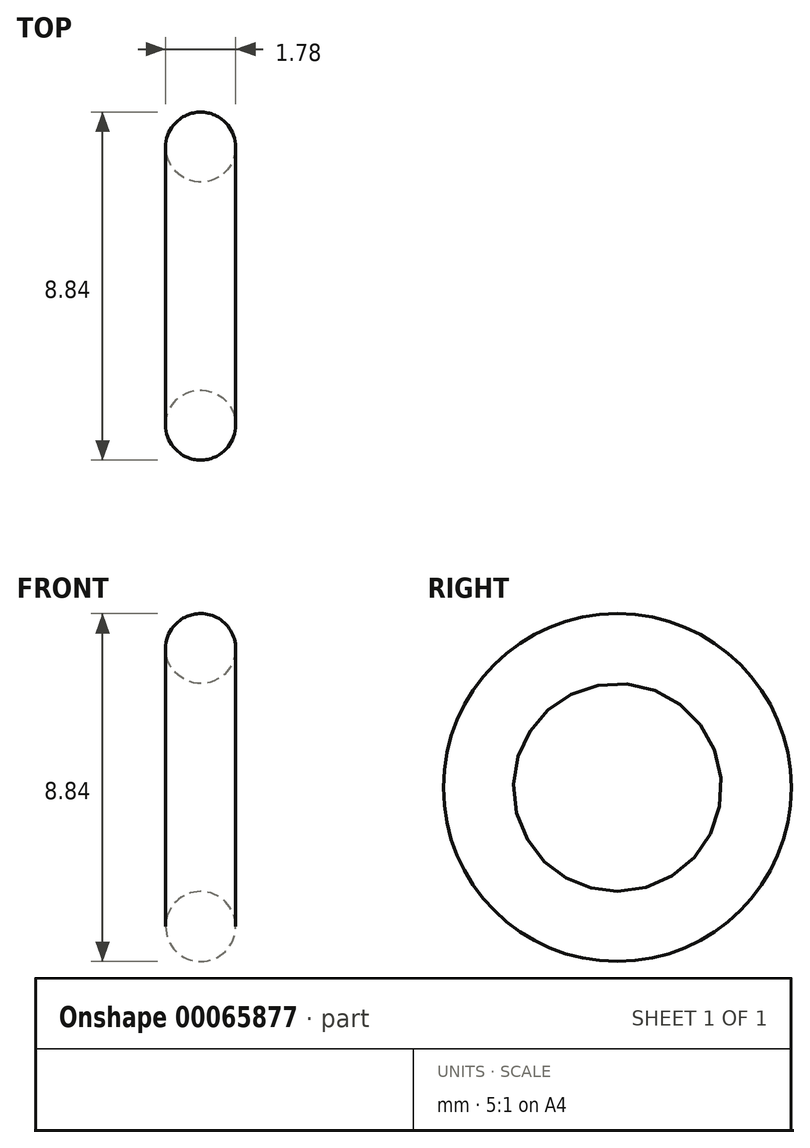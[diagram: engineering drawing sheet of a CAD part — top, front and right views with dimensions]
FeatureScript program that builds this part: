
annotation { "Feature Type Name" : "Feature", "Feature Type Description" : "" }
export const myFeature = defineFeature(function(context is Context, id is Id, definition is map)
    precondition{}
    {
        {
            var Q0;
            Q0=qCreatedBy(makeId("Front.planeOp"),FACE);
            var sketch = newSketch(context, id + "F0", { "sketchPlane" : qUnion([Q0])});
            skLineSegment(sketch, "E0", {"start": v(0, 0) * mm, "end": v(-6.06, 0) * mm, "construction": true});
            skCircle(sketch, "E1", {"center": v(0, 3.53) * mm, "radius": 0.89 * mm});
            skSolve(sketch);
        }
        {
            var Q0;
            Q0=makeQuery(id+"F0.imprint","IMPRINT",FACE,{"disambiguationData":[TD([[makeQuery(id+"F0.imprint","IMPRINT",EDGE,{"derivedFrom":sQuery(id+"F0.wireOp",EDGE,"E1")}),1.0]])]});
            var Q1;
            Q1=sQuery(id+"F0.wireOp",EDGE,"E0");
            revolve(context, id + "F1", {"entities" : qUnion([Q0]), "axis" : qUnion([Q1]), "revolveType" : RevolveType.FULL});
        }
    });
